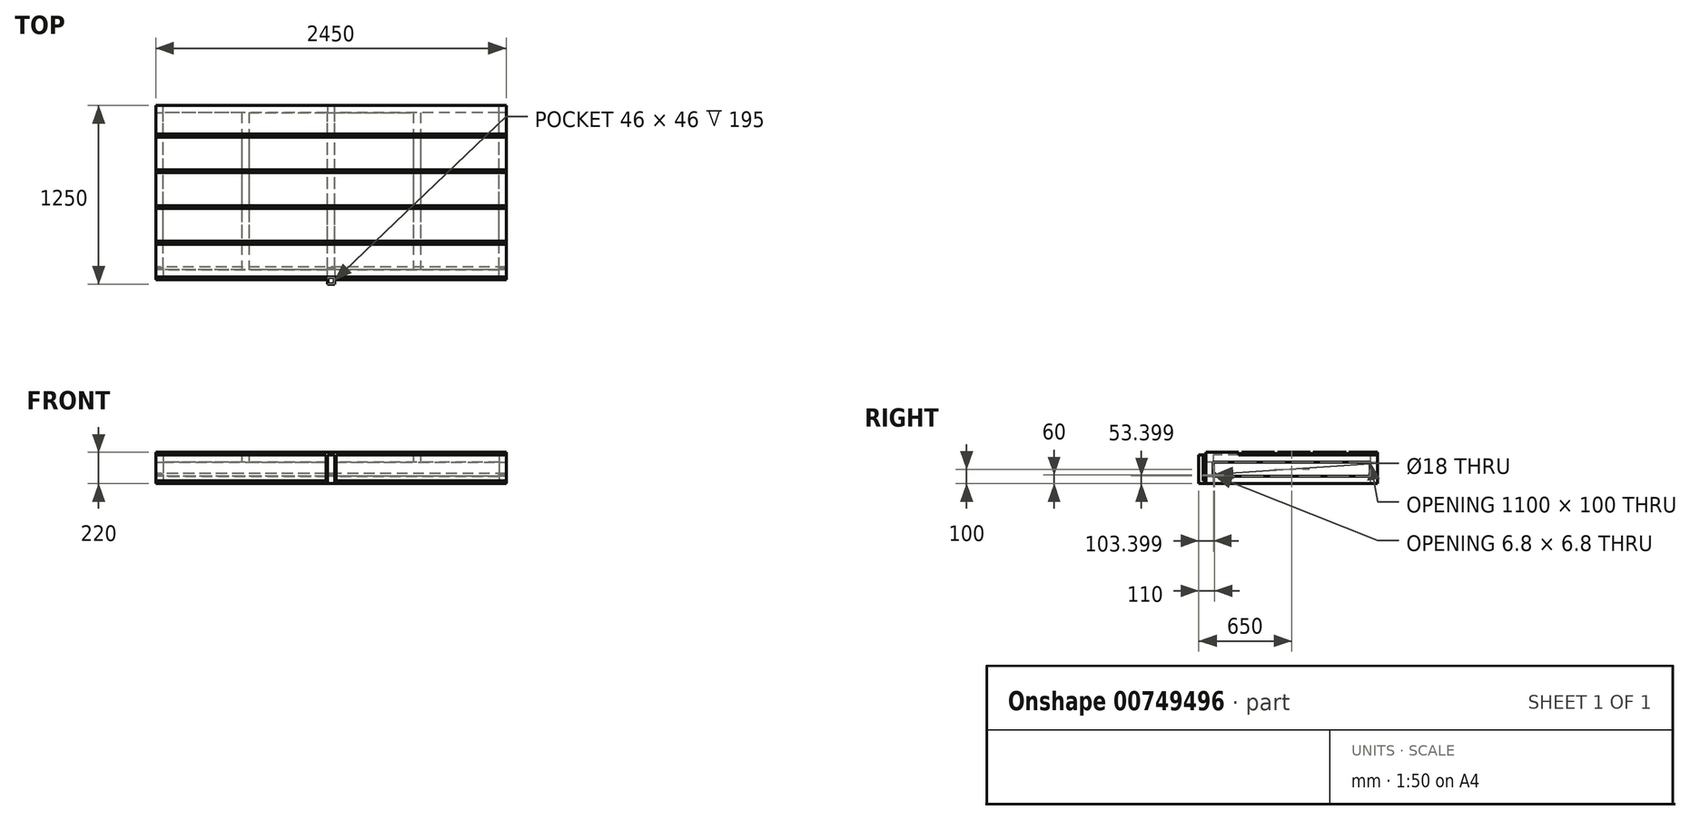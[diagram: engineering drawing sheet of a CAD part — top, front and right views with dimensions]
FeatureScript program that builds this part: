
annotation { "Feature Type Name" : "Feature", "Feature Type Description" : "" }
export const myFeature = defineFeature(function(context is Context, id is Id, definition is map)
    precondition{}
    {
        {
            var Q0;
            Q0=qCreatedBy(makeId("Top.planeOp"),FACE);
            var sketch = newSketch(context, id + "F0", { "sketchPlane" : qUnion([Q0])});
            skLineSegment(sketch, "E0.bottom", {"start": v(1225, -600) * mm, "end": v(-1225, -600) * mm});
            skLineSegment(sketch, "E0.top", {"start": v(1225, 600) * mm, "end": v(-1225, 600) * mm});
            skLineSegment(sketch, "E0.left", {"start": v(1225, -600) * mm, "end": v(1225, 600) * mm});
            skLineSegment(sketch, "E0.right", {"start": v(-1225, -600) * mm, "end": v(-1225, 600) * mm});
            skPoint(sketch, "E0.middle", {"position": v(0, 0) * mm});
            skLineSegment(sketch, "E1.0", {"start": v(1225, 550) * mm, "end": v(-1225, 550) * mm});
            skLineSegment(sketch, "E2.0", {"start": v(1227.5, -600) * mm, "end": v(1227.5, 600) * mm});
            skLineSegment(sketch, "E3.0", {"start": v(1175, -600) * mm, "end": v(1175, 600) * mm});
            skLineSegment(sketch, "E4.0", {"start": v(1225, -550) * mm, "end": v(-1225, -550) * mm});
            skLineSegment(sketch, "E5.0", {"start": v(-1175, -600) * mm, "end": v(-1175, 600) * mm});
            skLineSegment(sketch, "E6", {"start": v(0, 0) * mm, "end": v(0, 550) * mm});
            skLineSegment(sketch, "E7", {"start": v(0, 0) * mm, "end": v(0, -550) * mm});
            skLineSegment(sketch, "E8.0", {"start": v(25, 0) * mm, "end": v(25, 550) * mm});
            skLineSegment(sketch, "E9.0", {"start": v(-25, 0) * mm, "end": v(-25, 550) * mm});
            skLineSegment(sketch, "E10.0", {"start": v(-25, 0) * mm, "end": v(-25, -550) * mm});
            skLineSegment(sketch, "E11.0", {"start": v(25, 0) * mm, "end": v(25, -550) * mm});
            skSolve(sketch);
        }
        {
            var Q0;
            Q0=qSketchRegion(id+"F0",true);
            var Q1;
            {var subQ1=sQuery(id+"F0.wireOp",EDGE,"E6");Q1=makeQuery(id+"F0.imprint","IMPRINT",FACE,{"disambiguationData":[TD([[makeQuery(id+"F0.imprint","IMPRINT",EDGE,{"derivedFrom":subQ1}),-1.0]])]});}
            var Q2;
            {var subQ3=sQuery(id+"F0.wireOp",EDGE,"E6");Q2=makeQuery(id+"F0.imprint","IMPRINT",FACE,{"disambiguationData":[TD([[makeQuery(id+"F0.imprint","IMPRINT",EDGE,{"derivedFrom":subQ3}),1.0]])]});}
            extrude(context, id + "F1", {"entities" : qUnion([Q0, Q1, Q2]), "depth" : 50 * mm, "offsetDistance" : 25 * mm});
        }
        {
            var Q0;
            Q0=makeQuery(id+"F1.opExtrude","CAP_FACE",FACE,{"disambiguationData":[OSD([sQuery(id+"F0.wireOp",EDGE,"E0.bottom"),sQuery(id+"F0.wireOp",EDGE,"E0.top"),sQuery(id+"F0.wireOp",EDGE,"E0.left"),sQuery(id+"F0.wireOp",EDGE,"E0.right"),sQuery(id+"F0.wireOp",EDGE,"E1.0"),sQuery(id+"F0.wireOp",EDGE,"E3.0"),sQuery(id+"F0.wireOp",EDGE,"E4.0"),sQuery(id+"F0.wireOp",EDGE,"E5.0"),sQuery(id+"F0.wireOp",EDGE,"E8.0"),sQuery(id+"F0.wireOp",EDGE,"E9.0"),sQuery(id+"F0.wireOp",EDGE,"E10.0"),sQuery(id+"F0.wireOp",EDGE,"E11.0")])],"isStart":false});
            var sketch = newSketch(context, id + "F2", { "sketchPlane" : qUnion([Q0])});
            skLineSegment(sketch, "E12", {"start": v(-25, 550) * mm, "end": v(25, 550) * mm});
            skLineSegment(sketch, "E13", {"start": v(25, 550) * mm, "end": v(25, 600) * mm});
            skLineSegment(sketch, "E14", {"start": v(25, 600) * mm, "end": v(-25, 600) * mm});
            skLineSegment(sketch, "E15", {"start": v(-25, 600) * mm, "end": v(-25, 550) * mm});
            skLineSegment(sketch, "E16", {"start": v(-1175, 550) * mm, "end": v(-1175, 600) * mm});
            skLineSegment(sketch, "E17", {"start": v(-1175, 600) * mm, "end": v(-1225, 600) * mm});
            skLineSegment(sketch, "E18", {"start": v(-1225, 600) * mm, "end": v(-1225, 550) * mm});
            skLineSegment(sketch, "E19", {"start": v(-1225, 550) * mm, "end": v(-1175, 550) * mm});
            skLineSegment(sketch, "E20", {"start": v(-1175, -550) * mm, "end": v(-1175, -600) * mm});
            skLineSegment(sketch, "E21", {"start": v(-1175, -600) * mm, "end": v(-1225, -600) * mm});
            skLineSegment(sketch, "E22", {"start": v(-1225, -600) * mm, "end": v(-1225, -550) * mm});
            skLineSegment(sketch, "E23", {"start": v(-1225, -550) * mm, "end": v(-1175, -550) * mm});
            skLineSegment(sketch, "E24", {"start": v(-25, -550) * mm, "end": v(25, -550) * mm});
            skLineSegment(sketch, "E25", {"start": v(25, -550) * mm, "end": v(25, -600) * mm});
            skLineSegment(sketch, "E26", {"start": v(25, -600) * mm, "end": v(-25, -600) * mm});
            skPoint(sketch, "E26.endSnap0", {"position": v(0, -600) * mm});
            skLineSegment(sketch, "E27", {"start": v(-25, -600) * mm, "end": v(-25, -550) * mm});
            skLineSegment(sketch, "E28", {"start": v(1175, -550) * mm, "end": v(1225, -550) * mm});
            skLineSegment(sketch, "E29", {"start": v(1225, -550) * mm, "end": v(1225, -600) * mm});
            skLineSegment(sketch, "E30", {"start": v(1225, -600) * mm, "end": v(1175, -600) * mm});
            skLineSegment(sketch, "E31", {"start": v(1175, -600) * mm, "end": v(1175, -550) * mm});
            skLineSegment(sketch, "E32", {"start": v(1175, 550) * mm, "end": v(1175, 600) * mm});
            skLineSegment(sketch, "E33", {"start": v(1175, 600) * mm, "end": v(1225, 600) * mm});
            skLineSegment(sketch, "E34", {"start": v(1225, 600) * mm, "end": v(1225, 550) * mm});
            skLineSegment(sketch, "E35", {"start": v(1225, 550) * mm, "end": v(1175, 550) * mm});
            skSolve(sketch);
        }
        {
            var Q0;
            Q0=qSketchRegion(id+"F2",true);
            extrude(context, id + "F3", {"entities" : qUnion([Q0]), "operationType" : NewBodyOperationType.ADD, "depth" : 100 * mm, "offsetDistance" : 25 * mm});
        }
        {
            var Q0;
            Q0=makeQuery(id+"F3.opExtrude","CAP_FACE",FACE,{"disambiguationData":[OSD([sQuery(id+"F2.wireOp",EDGE,"E12"),sQuery(id+"F2.wireOp",EDGE,"E13"),sQuery(id+"F2.wireOp",EDGE,"E14"),sQuery(id+"F2.wireOp",EDGE,"E15")])],"isStart":false});
            var sketch = newSketch(context, id + "F4", { "sketchPlane" : qUnion([Q0])});
            skLineSegment(sketch, "E36.bottom", {"start": v(-1225, 600) * mm, "end": v(1225, 600) * mm});
            skLineSegment(sketch, "E36.top", {"start": v(-1225, -600) * mm, "end": v(1225, -600) * mm});
            skLineSegment(sketch, "E36.left", {"start": v(-1225, 600) * mm, "end": v(-1225, -600) * mm});
            skLineSegment(sketch, "E36.right", {"start": v(1225, 600) * mm, "end": v(1225, -600) * mm});
            skLineSegment(sketch, "E37.bottom", {"start": v(1175, -550) * mm, "end": v(-1175, -550) * mm});
            skLineSegment(sketch, "E37.top", {"start": v(1175, 550) * mm, "end": v(-1175, 550) * mm});
            skLineSegment(sketch, "E37.left", {"start": v(1175, -550) * mm, "end": v(1175, 550) * mm});
            skLineSegment(sketch, "E37.right", {"start": v(-1175, -550) * mm, "end": v(-1175, 550) * mm});
            skLineSegment(sketch, "E38.bottom", {"start": v(-25, 550) * mm, "end": v(25, 550) * mm});
            skLineSegment(sketch, "E38.top", {"start": v(-25, -550) * mm, "end": v(25, -550) * mm});
            skLineSegment(sketch, "E38.left", {"start": v(-25, 550) * mm, "end": v(-25, -550) * mm});
            skLineSegment(sketch, "E38.right", {"start": v(25, 550) * mm, "end": v(25, -550) * mm});
            skLineSegment(sketch, "E39", {"start": v(-25, 550) * mm, "end": v(-1175, 550) * mm});
            skLineSegment(sketch, "E40", {"start": v(-600, 550) * mm, "end": v(-600, -550) * mm});
            skLineSegment(sketch, "E41.0", {"start": v(-625, 550) * mm, "end": v(-625, -550) * mm});
            skLineSegment(sketch, "E42.0", {"start": v(-575, 550) * mm, "end": v(-575, -550) * mm});
            skLineSegment(sketch, "E43", {"start": v(25, 550) * mm, "end": v(1175, 550) * mm});
            skLineSegment(sketch, "E44", {"start": v(600, 550) * mm, "end": v(600, -550) * mm});
            skLineSegment(sketch, "E45.0", {"start": v(575, 550) * mm, "end": v(575, -550) * mm});
            skLineSegment(sketch, "E46.0", {"start": v(625, 550) * mm, "end": v(625, -550) * mm});
            skSolve(sketch);
        }
        {
            var Q0;
            Q0=qSketchRegion(id+"F4",true);
            var Q1;
            {var subQ0=sQuery(id+"F4.wireOp",EDGE,"E40");Q1=makeQuery(id+"F4.imprint","IMPRINT",FACE,{"disambiguationData":[TD([[makeQuery(id+"F4.imprint","IMPRINT",EDGE,{"derivedFrom":subQ0}),1.0]])]});}
            var Q2;
            {var subQ0=sQuery(id+"F4.wireOp",EDGE,"E40");Q2=makeQuery(id+"F4.imprint","IMPRINT",FACE,{"disambiguationData":[TD([[makeQuery(id+"F4.imprint","IMPRINT",EDGE,{"derivedFrom":subQ0}),-1.0]])]});}
            var Q3;
            {var subQ0=sQuery(id+"F4.wireOp",EDGE,"E44");Q3=makeQuery(id+"F4.imprint","IMPRINT",FACE,{"disambiguationData":[TD([[makeQuery(id+"F4.imprint","IMPRINT",EDGE,{"derivedFrom":subQ0}),1.0]])]});}
            var Q4;
            {var subQ0=sQuery(id+"F4.wireOp",EDGE,"E44");Q4=makeQuery(id+"F4.imprint","IMPRINT",FACE,{"disambiguationData":[TD([[makeQuery(id+"F4.imprint","IMPRINT",EDGE,{"derivedFrom":subQ0}),-1.0]])]});}
            var Q5;
            Q5=makeQuery(id+"F4.imprint","IMPRINT",FACE,{"disambiguationData":[TD([[makeQuery(id+"F4.imprint","IMPRINT",EDGE,{"derivedFrom":sQuery(id+"F4.wireOp",EDGE,"E38.bottom")}),-1.0]])]});
            extrude(context, id + "F5", {"entities" : qUnion([Q0, Q1, Q2, Q3, Q4, Q5]), "operationType" : NewBodyOperationType.ADD, "depth" : 50 * mm, "offsetDistance" : 25 * mm});
        }
        {
            var Q0;
            Q0=makeQuery(id+"F5.boolean.opBoolean","MERGE",FACE,{"derivedFrom":[makeQuery(id+"F3.boolean.opBoolean","MERGE",FACE,{"derivedFrom":[makeQuery(id+"F1.opExtrude","SWEPT_FACE",FACE,{"disambiguationData":[OSD([sQuery(id+"F0.wireOp",EDGE,"E0.right")])]}),makeQuery(id+"F3.opExtrude","SWEPT_FACE",FACE,{"disambiguationData":[OSD([sQuery(id+"F2.wireOp",EDGE,"E18")])]}),makeQuery(id+"F3.opExtrude","SWEPT_FACE",FACE,{"disambiguationData":[OSD([sQuery(id+"F2.wireOp",EDGE,"E22")])]})]}),makeQuery(id+"F5.opExtrude","SWEPT_FACE",FACE,{"disambiguationData":[OSD([sQuery(id+"F4.wireOp",EDGE,"E36.left")])]})]});
            var sketch = newSketch(context, id + "F6", { "sketchPlane" : qUnion([Q0])});
            skLineSegment(sketch, "E47", {"start": v(550, 50) * mm, "end": v(550, 60) * mm});
            skLineSegment(sketch, "E48", {"start": v(550, 60) * mm, "end": v(540, 60) * mm});
            skCircle(sketch, "E49", {"center": v(540, 60) * mm, "radius": 10.5 * mm});
            skCircle(sketch, "E50", {"center": v(540, 60) * mm, "radius": 9 * mm});
            skSolve(sketch);
        }
        {
            var Q0;
            Q0=qSketchRegion(id+"F6",true);
            extrude(context, id + "F7", {"entities" : qUnion([Q0]), "operationType" : NewBodyOperationType.ADD, "oppositeDirection" : true, "depth" : 2450 * mm, "offsetDistance" : 25 * mm});
        }
        {
            var Q0;
            Q0=makeQuery(id+"F5.boolean.opBoolean","MERGE",FACE,{"derivedFrom":[makeQuery(id+"F3.boolean.opBoolean","MERGE",FACE,{"derivedFrom":[makeQuery(id+"F1.opExtrude","SWEPT_FACE",FACE,{"disambiguationData":[OSD([sQuery(id+"F0.wireOp",EDGE,"E0.bottom")])]}),makeQuery(id+"F3.opExtrude","SWEPT_FACE",FACE,{"disambiguationData":[OSD([sQuery(id+"F2.wireOp",EDGE,"E21")])]}),makeQuery(id+"F3.opExtrude","SWEPT_FACE",FACE,{"disambiguationData":[OSD([sQuery(id+"F2.wireOp",EDGE,"E26")])]}),makeQuery(id+"F3.opExtrude","SWEPT_FACE",FACE,{"disambiguationData":[OSD([sQuery(id+"F2.wireOp",EDGE,"E30")])]})]}),makeQuery(id+"F5.opExtrude","SWEPT_FACE",FACE,{"disambiguationData":[OSD([sQuery(id+"F4.wireOp",EDGE,"E36.top")])]})]});
            var sketch = newSketch(context, id + "F8", { "sketchPlane" : qUnion([Q0])});
            skLineSegment(sketch, "E51.bottom", {"start": v(1225, 200) * mm, "end": v(-1275, 200) * mm});
            skLineSegment(sketch, "E51.top", {"start": v(1225, 20) * mm, "end": v(-1275, 20) * mm});
            skLineSegment(sketch, "E51.left", {"start": v(1225, 200) * mm, "end": v(1225, 20) * mm});
            skLineSegment(sketch, "E51.right", {"start": v(-1275, 200) * mm, "end": v(-1275, 20) * mm});
            skLineSegment(sketch, "E52", {"start": v(-1225, 200) * mm, "end": v(-1275, 200) * mm});
            skSolve(sketch);
        }
        {
            var Q0;
            Q0=qSketchRegion(id+"F8",true);
            extrude(context, id + "F9", {"entities" : qUnion([Q0]), "depth" : 20 * mm, "offsetDistance" : 25 * mm});
        }
        {
            var Q0;
            Q0=makeQuery(id+"F5.opExtrude","CAP_FACE",FACE,{"disambiguationData":[OSD([sQuery(id+"F4.wireOp",EDGE,"E36.bottom"),sQuery(id+"F4.wireOp",EDGE,"E36.top"),sQuery(id+"F4.wireOp",EDGE,"E36.left"),sQuery(id+"F4.wireOp",EDGE,"E36.right"),sQuery(id+"F4.wireOp",EDGE,"E37.bottom"),sQuery(id+"F4.wireOp",EDGE,"E37.left"),sQuery(id+"F4.wireOp",EDGE,"E37.right"),sQuery(id+"F4.wireOp",EDGE,"E38.left"),sQuery(id+"F4.wireOp",EDGE,"E38.right"),sQuery(id+"F4.wireOp",EDGE,"E39"),sQuery(id+"F4.wireOp",EDGE,"E41.0"),sQuery(id+"F4.wireOp",EDGE,"E42.0"),sQuery(id+"F4.wireOp",EDGE,"E43"),sQuery(id+"F4.wireOp",EDGE,"E45.0"),sQuery(id+"F4.wireOp",EDGE,"E46.0")])],"isStart":false});
            var sketch = newSketch(context, id + "F10", { "sketchPlane" : qUnion([Q0])});
            skLineSegment(sketch, "E53.bottom", {"start": v(1225, 600) * mm, "end": v(-1275, 600) * mm});
            skLineSegment(sketch, "E53.top", {"start": v(1225, -600) * mm, "end": v(-1275, -600) * mm});
            skLineSegment(sketch, "E53.left", {"start": v(1225, 600) * mm, "end": v(1225, -600) * mm});
            skLineSegment(sketch, "E53.right", {"start": v(-1275, 600) * mm, "end": v(-1275, -600) * mm});
            skSolve(sketch);
        }
        {
            var Q0;
            Q0=qSketchRegion(id+"F10",true);
            extrude(context, id + "F11", {"entities" : qUnion([Q0]), "depth" : 20 * mm, "offsetDistance" : 25 * mm});
        }
        {
            var Q0;
            Q0=makeQuery(id+"F9.opExtrude","SWEPT_FACE",FACE,{"disambiguationData":[OSD([sQuery(id+"F8.wireOp",EDGE,"E51.right")])]});
            extrude(context, id + "F12", {"entities" : qUnion([Q0]), "operationType" : NewBodyOperationType.REMOVE, "oppositeDirection" : true, "depth" : 110 * mm, "offsetDistance" : 25 * mm});
        }
        {
            var Q0;
            Q0=makeQuery(id+"F11.opExtrude","SWEPT_FACE",FACE,{"disambiguationData":[OSD([sQuery(id+"F10.wireOp",EDGE,"E53.right")])]});
            var sketch = newSketch(context, id + "F13", { "sketchPlane" : qUnion([Q0])});
            skLineSegment(sketch, "E54.bottom", {"start": v(600, 200) * mm, "end": v(620.46, 200) * mm});
            skLineSegment(sketch, "E54.top", {"start": v(600, 220) * mm, "end": v(620.46, 220) * mm});
            skLineSegment(sketch, "E54.left", {"start": v(600, 200) * mm, "end": v(600, 220) * mm});
            skLineSegment(sketch, "E54.right", {"start": v(620.46, 200) * mm, "end": v(620.46, 220) * mm});
            skLineSegment(sketch, "E55.1.0.0", {"start": v(350, 220) * mm, "end": v(370.46, 220) * mm});
            skLineSegment(sketch, "E55.1.0.1", {"start": v(370.46, 200) * mm, "end": v(370.46, 220) * mm});
            skLineSegment(sketch, "E55.1.0.2", {"start": v(350, 200) * mm, "end": v(370.46, 200) * mm});
            skLineSegment(sketch, "E55.1.0.3", {"start": v(350, 200) * mm, "end": v(350, 220) * mm});
            skLineSegment(sketch, "E55.2.0.0", {"start": v(100, 220) * mm, "end": v(120.46, 220) * mm});
            skLineSegment(sketch, "E55.2.0.1", {"start": v(120.46, 200) * mm, "end": v(120.46, 220) * mm});
            skLineSegment(sketch, "E55.2.0.2", {"start": v(100, 200) * mm, "end": v(120.46, 200) * mm});
            skLineSegment(sketch, "E55.2.0.3", {"start": v(100, 200) * mm, "end": v(100, 220) * mm});
            skLineSegment(sketch, "E55.3.0.0", {"start": v(-150, 220) * mm, "end": v(-129.54, 220) * mm});
            skLineSegment(sketch, "E55.3.0.1", {"start": v(-129.54, 200) * mm, "end": v(-129.54, 220) * mm});
            skLineSegment(sketch, "E55.3.0.2", {"start": v(-150, 200) * mm, "end": v(-129.54, 200) * mm});
            skLineSegment(sketch, "E55.3.0.3", {"start": v(-150, 200) * mm, "end": v(-150, 220) * mm});
            skLineSegment(sketch, "E55.4.0.0", {"start": v(-400, 220) * mm, "end": v(-379.54, 220) * mm});
            skLineSegment(sketch, "E55.4.0.1", {"start": v(-379.54, 200) * mm, "end": v(-379.54, 220) * mm});
            skLineSegment(sketch, "E55.4.0.2", {"start": v(-400, 200) * mm, "end": v(-379.54, 200) * mm});
            skLineSegment(sketch, "E55.4.0.3", {"start": v(-400, 200) * mm, "end": v(-400, 220) * mm});
            skLineSegment(sketch, "E55.direction1", {"start": v(600, 200) * mm, "end": v(350, 200) * mm, "construction": true});
            skSolve(sketch);
        }
        {
            var Q0;
            Q0=qSketchRegion(id+"F13",true);
            var Q1;
            Q1=makeQuery(id+"F11.opExtrude","SWEPT_FACE",FACE,{"disambiguationData":[OSD([sQuery(id+"F10.wireOp",EDGE,"E53.left")])]});
            extrude(context, id + "F14", {"entities" : qUnion([Q0]), "operationType" : NewBodyOperationType.REMOVE, "endBound" : BoundingType.UP_TO_SURFACE, "oppositeDirection" : true, "depth" : 25 * mm, "endBoundEntityFace" : qUnion([Q1]), "offsetDistance" : 25 * mm});
        }
        {
            var Q0;
            Q0=makeQuery(id+"F12.boolean.opBoolean","COPY",FACE,{"derivedFrom":makeQuery(id+"F12.opExtrude","CAP_FACE",FACE,{"disambiguationData":[OSD([sQuery(id+"F8.wireOp",EDGE,"E51.right")])],"isStart":false})});
            var Q1;
            Q1=makeQuery(id+"F5.boolean.opBoolean","MERGE",FACE,{"derivedFrom":[makeQuery(id+"F3.boolean.opBoolean","MERGE",FACE,{"derivedFrom":[makeQuery(id+"F1.opExtrude","SWEPT_FACE",FACE,{"disambiguationData":[OSD([sQuery(id+"F0.wireOp",EDGE,"E0.right")])]}),makeQuery(id+"F3.opExtrude","SWEPT_FACE",FACE,{"disambiguationData":[OSD([sQuery(id+"F2.wireOp",EDGE,"E18")])]}),makeQuery(id+"F3.opExtrude","SWEPT_FACE",FACE,{"disambiguationData":[OSD([sQuery(id+"F2.wireOp",EDGE,"E22")])]})]}),makeQuery(id+"F5.opExtrude","SWEPT_FACE",FACE,{"disambiguationData":[OSD([sQuery(id+"F4.wireOp",EDGE,"E36.left")])]})]});
            extrude(context, id + "F15", {"entities" : qUnion([Q0]), "endBound" : BoundingType.UP_TO_SURFACE, "depth" : 25 * mm, "endBoundEntityFace" : qUnion([Q1]), "offsetDistance" : 25 * mm});
        }
        {
            var Q0;
            Q0=makeQuery(id+"F9.opExtrude","SWEPT_BODY",BODY,{"disambiguationData":[OSD([sQuery(id+"F8.wireOp",EDGE,"E51.bottom"),sQuery(id+"F8.wireOp",EDGE,"E51.top"),sQuery(id+"F8.wireOp",EDGE,"E51.left"),sQuery(id+"F8.wireOp",EDGE,"E51.right"),sQuery(id+"F8.wireOp",EDGE,"E52")])]});
            var Q1;
            Q1=makeQuery(id+"F15.opExtrude","SWEPT_BODY",BODY,{"disambiguationData":[OSD([sQuery(id+"F8.wireOp",EDGE,"E51.right")])]});
            booleanBodies(context, id + "F16", {"operationType" : BooleanOperationType.UNION, "tools" : qUnion([Q0, Q1])});
        }
        {
            var Q0;
            Q0=makeQuery(id+"F11.opExtrude","SWEPT_FACE",FACE,{"disambiguationData":[OSD([sQuery(id+"F10.wireOp",EDGE,"E53.top")])]});
            var sketch = newSketch(context, id + "F17", { "sketchPlane" : qUnion([Q0])});
            skLineSegment(sketch, "E56.bottom", {"start": v(-1225, 200) * mm, "end": v(-1275, 200) * mm});
            skLineSegment(sketch, "E56.top", {"start": v(-1225, 220) * mm, "end": v(-1275, 220) * mm});
            skLineSegment(sketch, "E56.left", {"start": v(-1225, 200) * mm, "end": v(-1225, 220) * mm});
            skLineSegment(sketch, "E56.right", {"start": v(-1275, 200) * mm, "end": v(-1275, 220) * mm});
            skSolve(sketch);
        }
        {
            var Q0;
            Q0=qSketchRegion(id+"F17",true);
            extrude(context, id + "F18", {"entities" : qUnion([Q0]), "operationType" : NewBodyOperationType.REMOVE, "endBound" : BoundingType.THROUGH_ALL, "oppositeDirection" : true, "depth" : 25 * mm, "offsetDistance" : 25 * mm});
        }
        {
            var Q0;
            Q0=makeQuery(id+"F1.opExtrude","CAP_FACE",FACE,{"disambiguationData":[OSD([sQuery(id+"F0.wireOp",EDGE,"E0.bottom"),sQuery(id+"F0.wireOp",EDGE,"E0.top"),sQuery(id+"F0.wireOp",EDGE,"E0.left"),sQuery(id+"F0.wireOp",EDGE,"E0.right"),sQuery(id+"F0.wireOp",EDGE,"E1.0"),sQuery(id+"F0.wireOp",EDGE,"E3.0"),sQuery(id+"F0.wireOp",EDGE,"E4.0"),sQuery(id+"F0.wireOp",EDGE,"E5.0"),sQuery(id+"F0.wireOp",EDGE,"E8.0"),sQuery(id+"F0.wireOp",EDGE,"E9.0"),sQuery(id+"F0.wireOp",EDGE,"E10.0"),sQuery(id+"F0.wireOp",EDGE,"E11.0")])],"isStart":true});
            var sketch = newSketch(context, id + "F19", { "sketchPlane" : qUnion([Q0])});
            skLineSegment(sketch, "E57.top", {"start": v(-25, 600) * mm, "end": v(25, 600) * mm});
            skLineSegment(sketch, "E58.top", {"start": v(-25, 650) * mm, "end": v(25, 650) * mm});
            skLineSegment(sketch, "E58.left", {"start": v(-25, 600) * mm, "end": v(-25, 650) * mm});
            skLineSegment(sketch, "E58.right", {"start": v(25, 600) * mm, "end": v(25, 650) * mm});
            skLineSegment(sketch, "E59", {"start": v(-25, 650) * mm, "end": v(-35, 650) * mm});
            skLineSegment(sketch, "E60", {"start": v(-35, 650) * mm, "end": v(-35, 600) * mm});
            skLineSegment(sketch, "E61", {"start": v(-35, 600) * mm, "end": v(-25, 600) * mm});
            skLineSegment(sketch, "E62", {"start": v(25, 650) * mm, "end": v(35, 650) * mm});
            skLineSegment(sketch, "E63", {"start": v(35, 650) * mm, "end": v(35, 600) * mm});
            skLineSegment(sketch, "E64", {"start": v(35, 600) * mm, "end": v(25, 600) * mm});
            skSolve(sketch);
        }
        {
            var Q0;
            Q0 = qSketchRegion(id + "F19", true);
            var Q1;
            {var subQ0=sQuery(id+"F8.wireOp",EDGE,"E52");Q1=makeQuery(id+"F16.opBoolean","MERGE",FACE,{"derivedFrom":[makeQuery(id+"F9.opExtrude","SWEPT_FACE",FACE,{"disambiguationData":[OSD([sQuery(id+"F8.wireOp",EDGE,"E51.bottom"),subQ0])]}),makeQuery(id+"F15.opExtrude","SWEPT_FACE",FACE,{"disambiguationData":[OSD([sQuery(id+"F8.wireOp",EDGE,"E51.right"),subQ0])]})]});}
            extrude(context, id + "F20", {"entities" : qUnion([Q0]), "operationType" : NewBodyOperationType.REMOVE, "endBound" : BoundingType.UP_TO_SURFACE, "oppositeDirection" : true, "depth" : 25 * mm, "endBoundEntityFace" : qUnion([Q1]), "offsetDistance" : 25 * mm});
        }
        {
            var Q0;
            Q0=makeQuery(id+"F1.opExtrude","CAP_FACE",FACE,{"disambiguationData":[OSD([sQuery(id+"F0.wireOp",EDGE,"E0.bottom"),sQuery(id+"F0.wireOp",EDGE,"E0.top"),sQuery(id+"F0.wireOp",EDGE,"E0.left"),sQuery(id+"F0.wireOp",EDGE,"E0.right"),sQuery(id+"F0.wireOp",EDGE,"E1.0"),sQuery(id+"F0.wireOp",EDGE,"E3.0"),sQuery(id+"F0.wireOp",EDGE,"E4.0"),sQuery(id+"F0.wireOp",EDGE,"E5.0"),sQuery(id+"F0.wireOp",EDGE,"E8.0"),sQuery(id+"F0.wireOp",EDGE,"E9.0"),sQuery(id+"F0.wireOp",EDGE,"E10.0"),sQuery(id+"F0.wireOp",EDGE,"E11.0")])],"isStart":true});
            var sketch = newSketch(context, id + "F21", { "sketchPlane" : qUnion([Q0])});
            skLineSegment(sketch, "E65", {"start": v(-25, 550) * mm, "end": v(-25, 600) * mm});
            skLineSegment(sketch, "E66", {"start": v(-25, 600) * mm, "end": v(-25, 650) * mm});
            skLineSegment(sketch, "E67", {"start": v(-25, 650) * mm, "end": v(25, 650) * mm});
            skLineSegment(sketch, "E68", {"start": v(25, 650) * mm, "end": v(25, 600) * mm});
            skLineSegment(sketch, "E69", {"start": v(25, 600) * mm, "end": v(-25, 600) * mm});
            skSolve(sketch);
        }
        {
            var Q0;
            Q0 = qSketchRegion(id + "F21", true);
            extrude(context, id + "F22", {"entities" : qUnion([Q0]), "operationType" : NewBodyOperationType.ADD, "oppositeDirection" : true, "depth" : 5 * mm, "offsetDistance" : 25 * mm});
        }
        {
            var Q0;
            Q0=makeQuery(id+"F22.opExtrude","CAP_FACE",FACE,{"disambiguationData":[OSD([sQuery(id+"F21.wireOp",EDGE,"E66"),sQuery(id+"F21.wireOp",EDGE,"E67"),sQuery(id+"F21.wireOp",EDGE,"E68"),sQuery(id+"F21.wireOp",EDGE,"E69")])],"isStart":false});
            var sketch = newSketch(context, id + "F23", { "sketchPlane" : qUnion([Q0])});
            skLineSegment(sketch, "E70.bottom", {"start": v(-25, -600) * mm, "end": v(25, -600) * mm});
            skLineSegment(sketch, "E70.top", {"start": v(-25, -650) * mm, "end": v(25, -650) * mm});
            skLineSegment(sketch, "E70.left", {"start": v(-25, -600) * mm, "end": v(-25, -650) * mm});
            skLineSegment(sketch, "E70.right", {"start": v(25, -600) * mm, "end": v(25, -650) * mm});
            skLineSegment(sketch, "E71.bottom", {"start": v(25, -650) * mm, "end": v(23, -650) * mm});
            skLineSegment(sketch, "E71.top", {"start": v(25, -648) * mm, "end": v(23, -648) * mm});
            skLineSegment(sketch, "E71.left", {"start": v(25, -650) * mm, "end": v(25, -648) * mm});
            skLineSegment(sketch, "E71.right", {"start": v(23, -650) * mm, "end": v(23, -648) * mm});
            skLineSegment(sketch, "E72.bottom", {"start": v(23, -648) * mm, "end": v(-23, -648) * mm});
            skLineSegment(sketch, "E72.top", {"start": v(23, -602) * mm, "end": v(-23, -602) * mm});
            skLineSegment(sketch, "E72.left", {"start": v(23, -648) * mm, "end": v(23, -602) * mm});
            skLineSegment(sketch, "E72.right", {"start": v(-23, -648) * mm, "end": v(-23, -602) * mm});
            skSolve(sketch);
        }
        {
            var Q0;
            Q0 = qSketchRegion(id + "F23", true);
            var Q1;
            {var subQ0=sQuery(id+"F8.wireOp",EDGE,"E51.right");var subQ1=sQuery(id+"F8.wireOp",EDGE,"E51.left");var subQ2=sQuery(id+"F8.wireOp",EDGE,"E52");var subQ4=sQuery(id+"F8.wireOp",EDGE,"E51.bottom");Q1=makeQuery(id+"F20.boolean.opBoolean","SPLIT",FACE,{"disambiguationData":[TD([makeQuery(id+"F9.opExtrude","SWEPT_FACE",FACE,{"disambiguationData":[OSD([subQ1])]})])],"derivedFrom":makeQuery(id+"F16.opBoolean","MERGE",FACE,{"derivedFrom":[makeQuery(id+"F9.opExtrude","SWEPT_FACE",FACE,{"disambiguationData":[OSD([subQ4,subQ2])]}),makeQuery(id+"F15.opExtrude","SWEPT_FACE",FACE,{"disambiguationData":[OSD([subQ0,subQ2])]})]})});}
            extrude(context, id + "F24", {"entities" : qUnion([Q0]), "operationType" : NewBodyOperationType.ADD, "endBound" : BoundingType.UP_TO_SURFACE, "depth" : 25 * mm, "endBoundEntityFace" : qUnion([Q1]), "offsetDistance" : 25 * mm});
        }
    });
